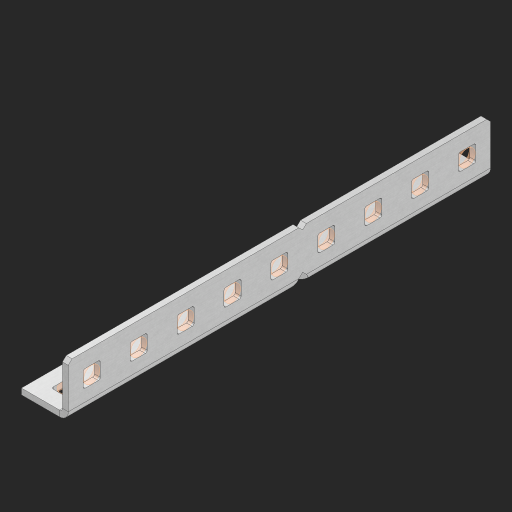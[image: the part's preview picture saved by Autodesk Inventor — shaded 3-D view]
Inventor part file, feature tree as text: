
AUTODESK INVENTOR PART (.ipt)
format: ipt  version: 2023 (Build 270158000, 158)  size: 558,080 bytes
history: native  units: in
note: dims shown in document units (in); Inventor stores cm internally (conversion verified against a paired STEP export)
features: other x23, extrude x17, sheet_metal_op x10, sketch x8, mirror x1, pattern_linear x1, chamfer x1
ambient origin geometry x8: Origin, YZ Plane, XZ Plane, XY Plane, X Axis, Y Axis, Z Axis, Center Point
bodies: Solid1 (feature_tree), Body (feature_tree)
feature tree (61):
  other  "Flange Pattern Plane"
  sheet_metal_op  "Flange Pattern"
  sheet_metal_op  "Body Pattern"
  other  "Arc Length"
  mirror  "Notch Mirror"
  pattern_linear  "Notch Pattern"  Spacing1=0.25in  [1 undecoded]
  chamfer  "End Chamfer"
  extrude  "Half Cut"  Depth=0.0625in
  sketch  "Sketch1"  dims[d0=1.5in]
  other  "Plate1"
  sketch  "Sketch2"  dims[d1=4.5in]
  other  "Plate2"
  sheet_metal_op  "Bend1"
  sheet_metal_op  "Corner1"
  sketch  "Sketch3"  dims[d2=0.0625in]
  other  "Flange Pattern Sketch"
  sketch  "Sketch7"  dims[d3=0.0625in]
  other  "Srf1"
  other  "Srf2"
  sketch  "Sketch8"  dims[d4=0.0312in]
  sketch  "Sketch9"  dims[d5=0.125in]
  other  "Srf91"
  sheet_metal_op  "Body Pattern Sketch"
  other  "Srf92"
  sketch  "Sketch13"  dims[d6=0.0625in]
  sketch  "Sketch14"  dims[d7=0.5in d8=90.0deg d9=0.0312in d10=0.25in d11=0.0625in d12=0.0625in d16=0.182in d17=0.02in d18=0.0625in d19=0.0in d20=0.25in d21=0.25in d46=0.172in d47=1.0in d48=0.0in d49=0.182in d50=0.02in d51=0.25in d52=0.25in d53=0.0625in d54=0.0in d55=0.172in d56=1.0in d57=0.0in d60=3.5433in d62=0.5in d63=0.3937in d65=0.5in d85=0.1473in d86=0.1782in d88=0.04in d89=0.0625in d90=0.0in d91=0.04in d92=0.0491in d95=2.5in d96=0.04in d97=0.25in d98=45.0deg d101=0.0in d102=2.497in d131=0.5in d132=3.5433in d134=0.5in d139=0.5in]
  other  "Srf856"
  other  "Srf1310"
  other  "Srf1311"
  other  "Srf1312"
  other  "Srf1376"
  other  "Srf1377"
  other  "Srf1728"
  other  "Srf1755"
  other  "Srf1878"
  other  "Srf1879"
  other  "Srf1880"
  other  "Srf1942"
  other  "Srf1943"
  other  "Srf1944"
  sheet_metal_op  "Flange Stamp"
  sheet_metal_op  "Flange Circle"
  sheet_metal_op  "Body Stamp"
  sheet_metal_op  "Body Circle"
  sheet_metal_op  "Notch"
  extrude  "ExtrusionSrf2"  Depth=0.0625in
  extrude  "ExtrusionSrf92"  Depth=0.5in
  extrude  "ExtrusionSrf856"  Depth=0.02in
  extrude  "ExtrusionSrf1310"  Depth=0.0625in
  extrude  "ExtrusionSrf1311"  TaperAngle=0.0deg  [1 undecoded]
  extrude  "ExtrusionSrf1312"  Depth=0.5in
  extrude  "ExtrusionSrf1376"  Depth=0.5in
  extrude  "ExtrusionSrf1377"  Depth=0.5in
  extrude  "ExtrusionSrf1728"  Depth=0.5in TaperAngle=0.0deg
  extrude  "ExtrusionSrf1755"  Depth=0.5in
  extrude  "ExtrusionSrf1878"  Depth=0.02in
  extrude  "ExtrusionSrf1879"  Depth=0.5in
  extrude  "ExtrusionSrf1880"  Depth=0.5in
  extrude  "ExtrusionSrf1942"  Depth=0.0625in
  extrude  "ExtrusionSrf1943"  TaperAngle=0.0deg  [1 undecoded]
  extrude  "ExtrusionSrf1944"  Depth=0.5in
note: 3 required parameter values undecoded (feature->parameter linkage not recoverable at this tier; creation-order binding heuristic only, values carry confidence <= 0.55)
